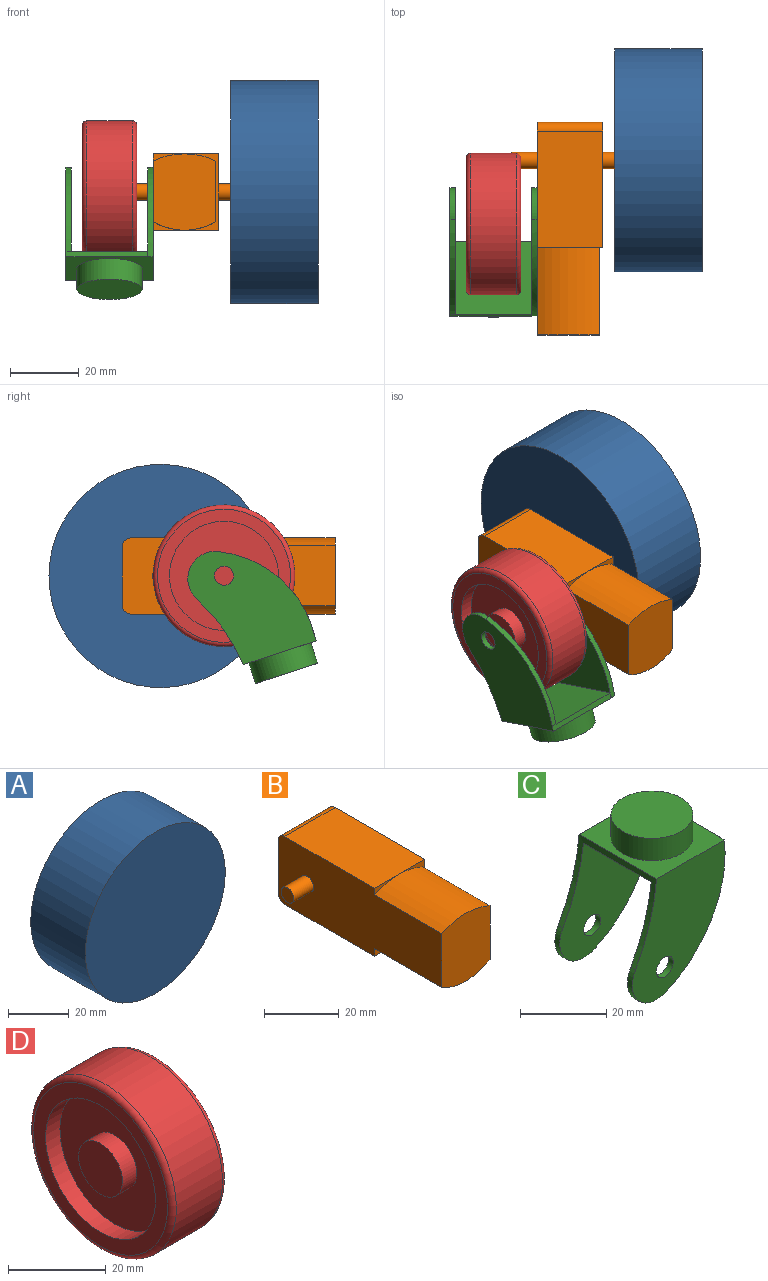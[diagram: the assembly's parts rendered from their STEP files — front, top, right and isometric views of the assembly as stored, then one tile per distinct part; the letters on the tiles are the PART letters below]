
ASSEMBLY  parts=4 mates=2
PART A: 3 faces, bbox 65x25.4x65 mm
  f0: cylinder r=32.5mm len=65mm, axis (0,1,0), area 5186.8mm2, adj f1,f2
  f1: plane 65x65mm, normal (0,-1,0), area 3318.3mm2, adj f0
  f2: plane 65x65mm, normal (0,1,0), area 3318.3mm2, adj f0
PART B: 18 faces, bbox 34.9x61.9x22.2 mm
  f0: plane 9.13x2.11mm, normal (0,-1,0), area 6.3mm2, adj f2,f3,f10
  f1: plane 22.23x9.92mm, normal (0,-1,0), area 31.3mm2, adj f2,f4,f5,f8,f9,f10
  f2: plane 33.97x19.05mm, normal (0,0,1), area 647.2mm2, adj f0,f1,f3,f5,f17
  f3: plane 61.91x22.23mm, normal (-1,0,0), area 1238.4mm2, adj f0,f2,f4,f6,f7,f8,f10,f11
  f4: plane 33.97x19.05mm, normal (0,0,-1), area 647.2mm2, adj f1,f3,f5,f6,f16
  f5: plane 36.51x22.23mm, normal (1,0,0), area 790.9mm2, adj f1,f2,f4,f7,f13,f16,f17
  f6: plane 9.13x2.5mm, normal (0,-1,0), area 7.4mm2, adj f3,f4,f8
  f7: plane 19.05x17.15mm, normal (0,1,0), area 326.6mm2, adj f3,f5,f16,f17
  f8: cylinder r=17.91mm len=25.4mm, axis (0,1,0), area 486.6mm2, adj f1,f3,f6,f9,f11
  f9: plane 25.4x17.62mm, normal (1,0,0), area 447.5mm2, adj f1,f8,f10,f11
  f10: cylinder r=20.84mm len=25.4mm, axis (0,1,0), area 480mm2, adj f0,f1,f3,f9,f11
  f11: plane 22.23x18.26mm, normal (0,-1,0), area 378.4mm2, adj f3,f8,f9,f10
  f12: plane 4.76x4.76mm, normal (1,0,0), area 17.8mm2, adj f13
  f13: cylinder r=2.38mm len=8.34mm, axis (-1,0,0), area 124.8mm2, adj f5,f12
  f14: cylinder r=2.38mm len=7.53mm, axis (-1,0,0), area 112.7mm2, adj f3,f15
  f15: plane 4.76x4.76mm, normal (-1,0,0), area 17.8mm2, adj f14
  f16: cylinder r=2.54mm len=19.05mm, axis (1,0,0), area 76mm2, adj f3,f4,f5,f7
  f17: cylinder r=2.54mm len=19.05mm, axis (-1,0,0), area 76mm2, adj f2,f3,f5,f7
PART C: 17 faces, bbox 30.4x25.4x40.6 mm
  f0: plane 22.54x22.23mm, normal (0,0,-1), area 501mm2, adj f1,f3,f7,f12
  f1: plane 32.68x30.42mm, normal (0,1,0), area 674.1mm2, adj f0,f3,f4,f5,f16
  f2: plane 25.4x22.39mm, normal (0,0,1), area 283.4mm2, adj f3,f5,f6,f7,f8,f9,f13
  f3: cylinder r=54.56mm len=25.4mm, axis (0,1,0), area 110.4mm2, adj f0,f1,f2,f4,f6,f8,f11,f12
  f4: cylinder r=7.94mm len=11.87mm, axis (0,1,0), area 32.4mm2, adj f1,f3,f5,f6
  f5: cylinder r=32.17mm len=33.35mm, axis (0,1,0), area 64.8mm2, adj f1,f2,f4,f6,f9
  f6: plane 34.26x30.42mm, normal (0,-1,0), area 709.7mm2, adj f2,f3,f4,f5,f16
  f7: plane 23.81x1.59mm, normal (1,0,0), area 37.8mm2, adj f0,f2,f8,f9,f10
  f8: plane 34.26x30.42mm, normal (0,1,0), area 709.8mm2, adj f2,f3,f7,f10,f11,f15
  f9: plane 1.59x0.16mm, normal (0,-1,0), area 0.1mm2, adj f2,f5,f7
  f10: cylinder r=32.17mm len=31.77mm, axis (0,1,0), area 62.3mm2, adj f7,f8,f11,f12
  f11: cylinder r=7.94mm len=11.87mm, axis (0,1,0), area 32.4mm2, adj f3,f8,f10,f12
  f12: plane 32.68x30.42mm, normal (0,-1,0), area 674.1mm2, adj f0,f3,f10,f11,f15
  f13: cylinder r=9.53mm len=19.05mm, axis (0,0,-1), area 380mm2, adj f2,f14
  f14: plane 19.05x19.05mm, normal (0,0,1), area 285mm2, adj f13
  f15: cylinder r=2.78mm len=5.56mm, axis (0,1,0), area 27.7mm2, adj f8,f12
  f16: cylinder r=2.78mm len=5.56mm, axis (0,1,0), area 27.7mm2, adj f1,f6
PART D: 13 faces, bbox 15.9x44.7x44.7 mm
  f0: cylinder r=15.88mm len=31.75mm, axis (1,0,0), area 411.7mm2, adj f2,f7
  f1: cylinder r=20.64mm len=41.28mm, axis (1,0,0), area 1729.1mm2, adj f4,f5
  f2: plane 38.74x38.74mm, normal (-1,0,0), area 386.7mm2, adj f0,f5
  f3: plane 38.74x38.74mm, normal (1,0,0), area 386.7mm2, adj f4,f6
  f4: torus R=19.37mm, axis (1,0,0), area 252.9mm2, adj f1,f3
  f5: torus R=19.37mm, axis (1,0,0), area 252.9mm2, adj f1,f2
  f6: cylinder r=15.88mm len=31.75mm, axis (1,0,0), area 411.7mm2, adj f3,f8
  f7: plane 31.75x31.75mm, normal (-1,0,0), area 665.1mm2, adj f0,f11
  f8: plane 31.75x31.75mm, normal (1,0,0), area 665.1mm2, adj f6,f10
  f9: plane 12.7x12.7mm, normal (1,0,0), area 126.7mm2, adj f10
  f10: cylinder r=6.35mm len=12.7mm, axis (-1,0,0), area 164.7mm2, adj f8,f9
  f11: cylinder r=6.35mm len=12.7mm, axis (-1,0,0), area 164.7mm2, adj f7,f12
  f12: plane 12.7x12.7mm, normal (-1,0,0), area 126.7mm2, adj f11
PLACE A rot(axis=(0.58,0.58,-0.58),120deg) t=(48.03,18.47,-0.07)mm
PLACE B t=(9.93,29.58,-0.25)mm
PLACE C rot(axis=(0.7,-0.7,0.11),167.2deg) t=(-1.59,2.59,-0.85)mm
PLACE D rot(axis=(0,-0.71,0.71),180deg) t=(-12.7,0,0)mm
MATE pin_slot D.f10 <-> C.f15  axis (1,0,0) through (-4.76,0,0)mm
MATE pin_slot B.f13 <-> A.f0  axis (1,0,0) through (27.39,18.47,-0.07)mm
